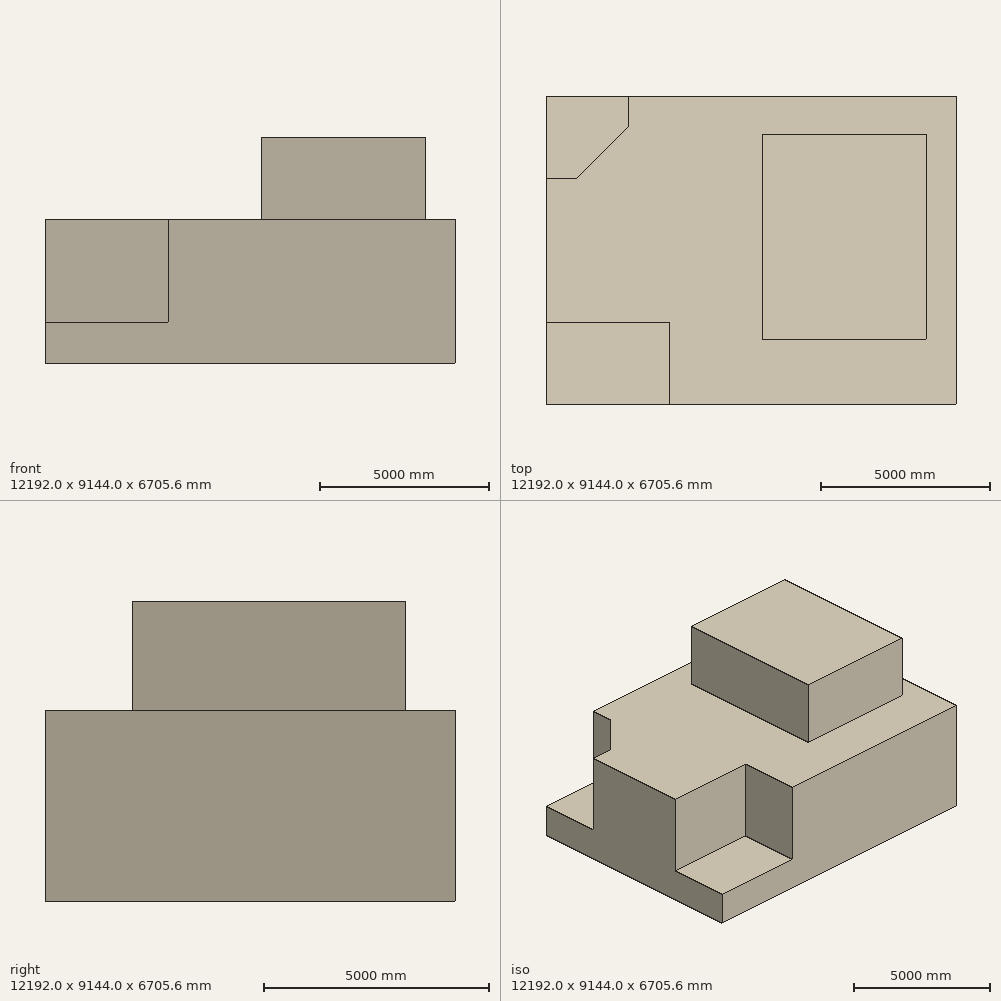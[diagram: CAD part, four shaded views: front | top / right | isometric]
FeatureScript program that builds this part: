
annotation { "Feature Type Name" : "Feature", "Feature Type Description" : "" }
export const myFeature = defineFeature(function(context is Context, id is Id, definition is map)
    precondition{}
    {
        {
            var Q0;
            Q0=qCreatedBy(makeId("Top.planeOp"),FACE);
            var sketch = newSketch(context, id + "F0", { "sketchPlane" : qUnion([Q0])});
            skLineSegment(sketch, "E0.bottom", {"start": v(-6096, 4572) * mm, "end": v(6096, 4572) * mm});
            skLineSegment(sketch, "E0.top", {"start": v(-6096, -4572) * mm, "end": v(6096, -4572) * mm});
            skLineSegment(sketch, "E0.left", {"start": v(-6096, 4572) * mm, "end": v(-6096, -4572) * mm});
            skLineSegment(sketch, "E0.right", {"start": v(6096, 4572) * mm, "end": v(6096, -4572) * mm});
            skSolve(sketch);
        }
        {
            var Q0;
            Q0=makeQuery(id+"F0.imprint","IMPRINT",FACE,{"disambiguationData":[TD([[makeQuery(id+"F0.imprint","IMPRINT",EDGE,{"derivedFrom":sQuery(id+"F0.wireOp",EDGE,"E0.bottom")}),-1.0]])]});
            extrude(context, id + "F1", {"entities" : qUnion([Q0]), "oppositeDirection" : true, "depth" : 1219.2 * mm, "offsetDistance" : 30.48 * mm});
        }
        {
            var Q0;
            Q0=makeQuery(id+"F1.opExtrude","CAP_FACE",FACE,{"disambiguationData":[OSD([sQuery(id+"F0.wireOp",EDGE,"E0.bottom"),sQuery(id+"F0.wireOp",EDGE,"E0.top"),sQuery(id+"F0.wireOp",EDGE,"E0.left"),sQuery(id+"F0.wireOp",EDGE,"E0.right")])],"isStart":true});
            var sketch = newSketch(context, id + "F2", { "sketchPlane" : qUnion([Q0])});
            skLineSegment(sketch, "E1", {"start": v(-3657.6, 4572) * mm, "end": v(-3657.6, 3657.6) * mm});
            skLineSegment(sketch, "E2", {"start": v(-3657.6, 3657.6) * mm, "end": v(-5181.6, 2133.6) * mm});
            skLineSegment(sketch, "E3", {"start": v(-5181.6, 2133.6) * mm, "end": v(-6096, 2133.6) * mm});
            skLineSegment(sketch, "E4", {"start": v(-6096, 2133.6) * mm, "end": v(-6096, -2133.6) * mm});
            skLineSegment(sketch, "E5", {"start": v(-6096, -2133.6) * mm, "end": v(-2438.4, -2133.6) * mm});
            skLineSegment(sketch, "E6", {"start": v(-2438.4, -2133.6) * mm, "end": v(-2438.4, -4572) * mm});
            skLineSegment(sketch, "E7", {"start": v(-2438.4, -4572) * mm, "end": v(6096, -4572) * mm});
            skLineSegment(sketch, "E8", {"start": v(6096, -4572) * mm, "end": v(6096, 4572) * mm});
            skLineSegment(sketch, "E9", {"start": v(6096, 4572) * mm, "end": v(-3657.6, 4572) * mm});
            skSolve(sketch);
        }
        {
            var Q0;
            Q0=makeQuery(id+"F2.imprint","IMPRINT",FACE,{"disambiguationData":[TD([[makeQuery(id+"F2.imprint","IMPRINT",EDGE,{"derivedFrom":sQuery(id+"F2.wireOp",EDGE,"E1")}),1.0]])]});
            extrude(context, id + "F3", {"entities" : qUnion([Q0]), "operationType" : NewBodyOperationType.ADD, "depth" : 3048 * mm, "offsetDistance" : 30.48 * mm});
        }
        {
            var Q0;
            Q0=makeQuery(id+"F3.opExtrude","CAP_FACE",FACE,{"disambiguationData":[OSD([sQuery(id+"F2.wireOp",EDGE,"E1"),sQuery(id+"F2.wireOp",EDGE,"E2"),sQuery(id+"F2.wireOp",EDGE,"E3"),sQuery(id+"F2.wireOp",EDGE,"E4"),sQuery(id+"F2.wireOp",EDGE,"E5"),sQuery(id+"F2.wireOp",EDGE,"E6"),sQuery(id+"F2.wireOp",EDGE,"E7"),sQuery(id+"F2.wireOp",EDGE,"E8"),sQuery(id+"F2.wireOp",EDGE,"E9")])],"isStart":false});
            var sketch = newSketch(context, id + "F4", { "sketchPlane" : qUnion([Q0])});
            skLineSegment(sketch, "E10.bottom", {"start": v(5198.93, 3454.66) * mm, "end": v(322.13, 3454.66) * mm});
            skLineSegment(sketch, "E10.top", {"start": v(5198.93, -2641.34) * mm, "end": v(322.13, -2641.34) * mm});
            skLineSegment(sketch, "E10.left", {"start": v(5198.93, 3454.66) * mm, "end": v(5198.93, -2641.34) * mm});
            skLineSegment(sketch, "E10.right", {"start": v(322.13, 3454.66) * mm, "end": v(322.13, -2641.34) * mm});
            skSolve(sketch);
        }
        {
            var Q0;
            Q0=makeQuery(id+"F4.imprint","IMPRINT",FACE,{"disambiguationData":[TD([[makeQuery(id+"F4.imprint","IMPRINT",EDGE,{"derivedFrom":sQuery(id+"F4.wireOp",EDGE,"E10.bottom")}),1.0]])]});
            var sketch = newSketch(context, id + "F5", { "sketchPlane" : qUnion([Q0])});
            skSolve(sketch);
        }
        {
            var Q0;
            Q0 = qSketchRegion(id + "F5", true);
            var Q1;
            Q1=makeQuery(id+"F5.imprint","IMPRINT",FACE,{"disambiguationData":[TD([[makeQuery(id+"F5.imprint","IMPRINT",EDGE,{"derivedFrom":makeQuery(id+"F4.imprint","IMPRINT",EDGE,{"derivedFrom":sQuery(id+"F4.wireOp",EDGE,"E10.bottom")})}),1.0]])]});
            extrude(context, id + "F6", {"entities" : qUnion([Q0, Q1]), "depth" : 2438.4 * mm, "offsetDistance" : 30.48 * mm});
        }
    });
